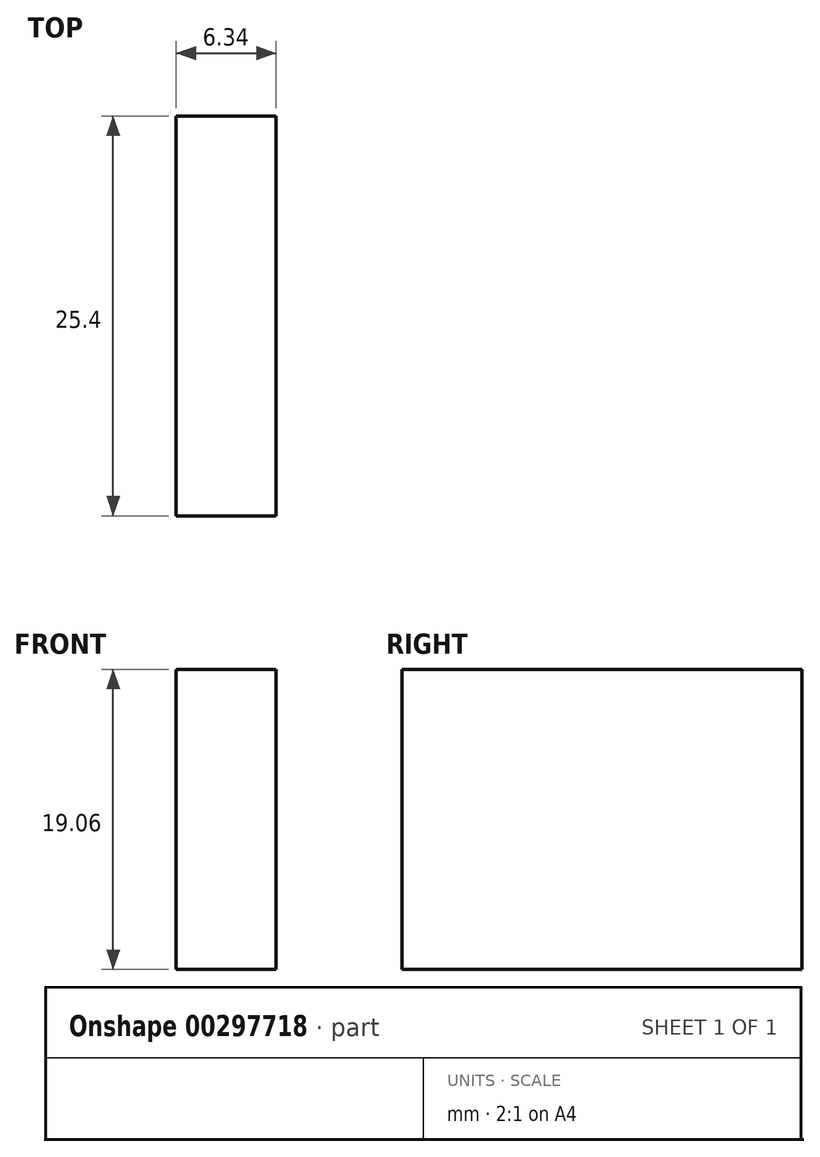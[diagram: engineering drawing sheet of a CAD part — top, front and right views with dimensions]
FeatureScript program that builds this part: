
annotation { "Feature Type Name" : "Feature", "Feature Type Description" : "" }
export const myFeature = defineFeature(function(context is Context, id is Id, definition is map)
    precondition{}
    {
        {
            var Q0;
            Q0=qCreatedBy(makeId("Front.planeOp"),FACE);
            var sketch = newSketch(context, id + "F0", { "sketchPlane" : qUnion([Q0])});
            skLineSegment(sketch, "E0.bottom", {"start": v(3.18, 9.53) * mm, "end": v(-3.17, 9.53) * mm});
            skLineSegment(sketch, "E0.top", {"start": v(3.17, -9.53) * mm, "end": v(-3.18, -9.53) * mm});
            skLineSegment(sketch, "E0.left", {"start": v(3.18, 9.53) * mm, "end": v(3.17, -9.53) * mm});
            skLineSegment(sketch, "E0.right", {"start": v(-3.17, 9.53) * mm, "end": v(-3.18, -9.53) * mm});
            skPoint(sketch, "E0.middle", {"position": v(0, 0) * mm});
            skSolve(sketch);
        }
        {
            var Q0;
            Q0 = qSketchRegion(id + "F0", true);
            extrude(context, id + "F1", {"entities" : qUnion([Q0]), "depth" : 25.4 * mm});
        }
    });
